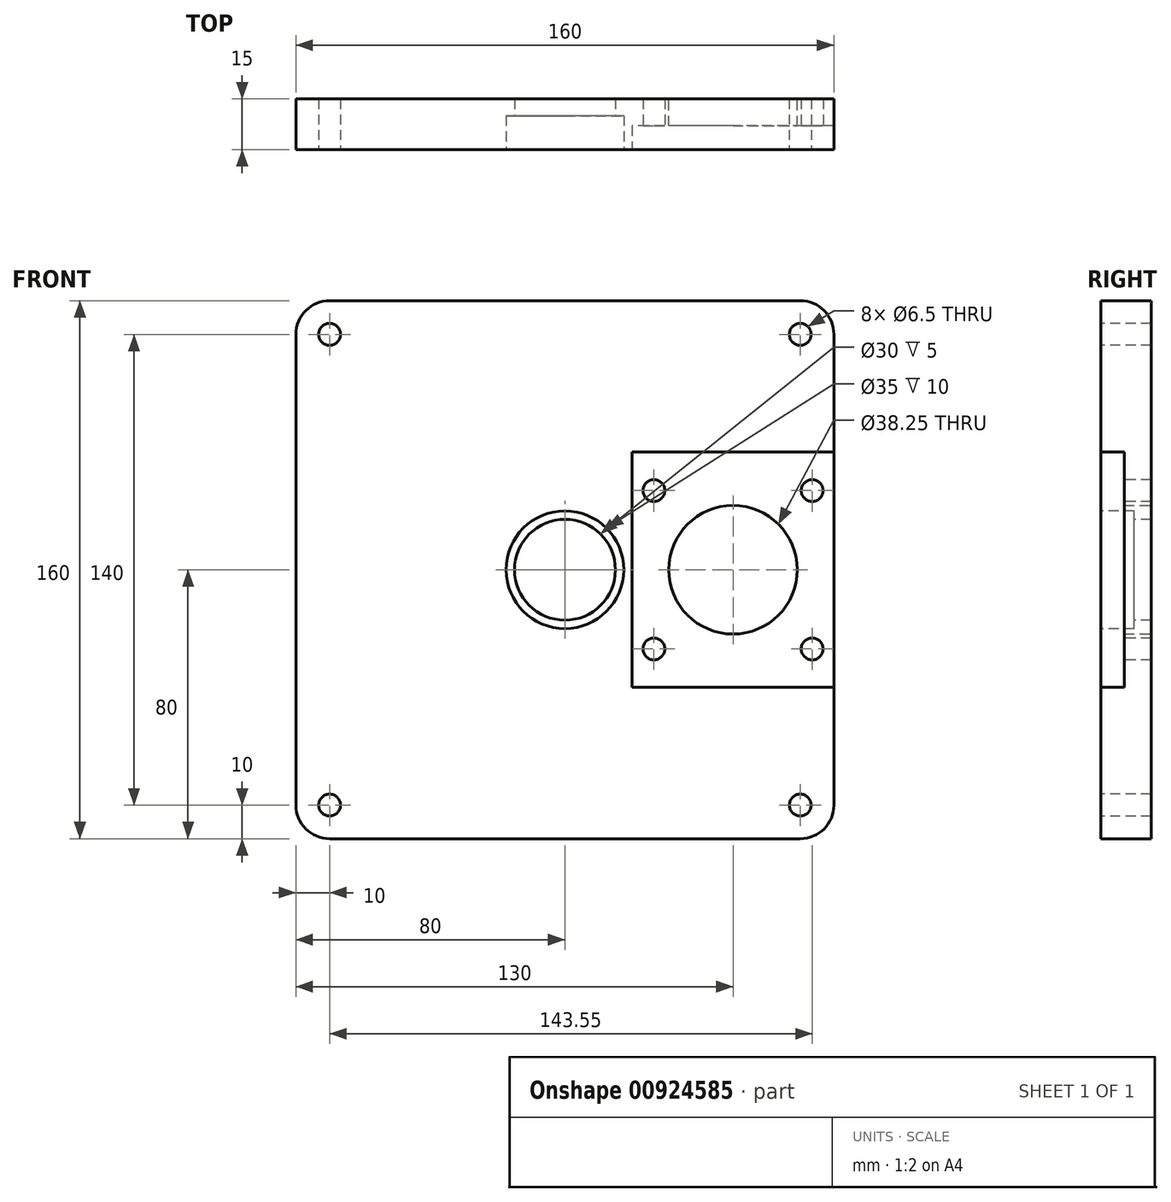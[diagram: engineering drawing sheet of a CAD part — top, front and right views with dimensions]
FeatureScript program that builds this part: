
annotation { "Feature Type Name" : "Feature", "Feature Type Description" : "" }
export const myFeature = defineFeature(function(context is Context, id is Id, definition is map)
    precondition{}
    {
        {
            var Q0;
            Q0=qCreatedBy(makeId("Front.planeOp"),FACE);
            var sketch = newSketch(context, id + "F0", { "sketchPlane" : qUnion([Q0])});
            skLineSegment(sketch, "E0.bottom", {"start": v(-80, 80) * mm, "end": v(80, 80) * mm});
            skLineSegment(sketch, "E0.top", {"start": v(-80, -80) * mm, "end": v(80, -80) * mm});
            skLineSegment(sketch, "E0.left", {"start": v(-80, 80) * mm, "end": v(-80, -80) * mm});
            skLineSegment(sketch, "E0.right", {"start": v(80, 80) * mm, "end": v(80, -80) * mm});
            skPoint(sketch, "E0.middle", {"position": v(0, 0) * mm});
            skSolve(sketch);
        }
        {
            var Q0;
            Q0=makeQuery(id+"F0.imprint","IMPRINT",FACE,{"disambiguationData":[TD([[makeQuery(id+"F0.imprint","IMPRINT",EDGE,{"derivedFrom":sQuery(id+"F0.wireOp",EDGE,"E0.bottom")}),-1.0]])]});
            extrude(context, id + "F1", {"entities" : qUnion([Q0]), "depth" : 15 * mm, "offsetDistance" : 25 * mm});
        }
        {
            var Q0;
            Q0=makeQuery(id+"F1.opExtrude","CAP_FACE",FACE,{"disambiguationData":[OSD([sQuery(id+"F0.wireOp",EDGE,"E0.bottom"),sQuery(id+"F0.wireOp",EDGE,"E0.top"),sQuery(id+"F0.wireOp",EDGE,"E0.left"),sQuery(id+"F0.wireOp",EDGE,"E0.right")])],"isStart":false});
            var sketch = newSketch(context, id + "F2", { "sketchPlane" : qUnion([Q0])});
            skCircle(sketch, "E1", {"center": v(0, 0) * mm, "radius": 15 * mm});
            skSolve(sketch);
        }
        {
            var Q0;
            Q0=makeQuery(id+"F2.imprint","IMPRINT",FACE,{"disambiguationData":[TD([[makeQuery(id+"F2.imprint","IMPRINT",EDGE,{"derivedFrom":sQuery(id+"F2.wireOp",EDGE,"E1")}),1.0]])]});
            extrude(context, id + "F3", {"entities" : qUnion([Q0]), "operationType" : NewBodyOperationType.REMOVE, "oppositeDirection" : true, "depth" : 25 * mm, "offsetDistance" : 25 * mm});
        }
        {
            var Q0;
            Q0=makeQuery(id+"F1.opExtrude","CAP_FACE",FACE,{"disambiguationData":[OSD([sQuery(id+"F0.wireOp",EDGE,"E0.bottom"),sQuery(id+"F0.wireOp",EDGE,"E0.top"),sQuery(id+"F0.wireOp",EDGE,"E0.left"),sQuery(id+"F0.wireOp",EDGE,"E0.right")])],"isStart":false});
            var sketch = newSketch(context, id + "F4", { "sketchPlane" : qUnion([Q0])});
            skCircle(sketch, "E2", {"center": v(0, 0) * mm, "radius": 17.5 * mm});
            skSolve(sketch);
        }
        {
            var Q0;
            Q0=makeQuery(id+"F4.imprint","IMPRINT",FACE,{"disambiguationData":[TD([[makeQuery(id+"F4.imprint","IMPRINT",EDGE,{"derivedFrom":sQuery(id+"F4.wireOp",EDGE,"E2")}),1.0]])]});
            extrude(context, id + "F5", {"entities" : qUnion([Q0]), "operationType" : NewBodyOperationType.REMOVE, "oppositeDirection" : true, "depth" : 10 * mm, "offsetDistance" : 25 * mm});
        }
        {
            var Q0;
            Q0=makeQuery(id+"F1.opExtrude","SWEPT_EDGE",EDGE,{"disambiguationData":[OSD([sQuery(id+"F0.wireOp",EDGE,"E0.bottom"),sQuery(id+"F0.wireOp",EDGE,"E0.right")])]});
            var Q1;
            Q1=makeQuery(id+"F1.opExtrude","SWEPT_EDGE",EDGE,{"disambiguationData":[OSD([sQuery(id+"F0.wireOp",EDGE,"E0.top"),sQuery(id+"F0.wireOp",EDGE,"E0.right")])]});
            var Q2;
            Q2=makeQuery(id+"F1.opExtrude","SWEPT_EDGE",EDGE,{"disambiguationData":[OSD([sQuery(id+"F0.wireOp",EDGE,"E0.top"),sQuery(id+"F0.wireOp",EDGE,"E0.left")])]});
            var Q3;
            Q3=makeQuery(id+"F1.opExtrude","SWEPT_EDGE",EDGE,{"disambiguationData":[OSD([sQuery(id+"F0.wireOp",EDGE,"E0.bottom"),sQuery(id+"F0.wireOp",EDGE,"E0.left")])]});
            fillet(context, id + "F6", {"entities" : qUnion([Q0, Q1, Q2, Q3]), "radius" : 10 * mm, "tangentPropagation" : true, "allowEdgeOverflow" : false});
        }
        {
            var Q0;
            Q0=makeQuery(id+"F1.opExtrude","CAP_FACE",FACE,{"disambiguationData":[OSD([sQuery(id+"F0.wireOp",EDGE,"E0.bottom"),sQuery(id+"F0.wireOp",EDGE,"E0.top"),sQuery(id+"F0.wireOp",EDGE,"E0.left"),sQuery(id+"F0.wireOp",EDGE,"E0.right")])],"isStart":false});
            var sketch = newSketch(context, id + "F7", { "sketchPlane" : qUnion([Q0])});
            skLineSegment(sketch, "E3.bottom", {"start": v(80, -35) * mm, "end": v(20, -35) * mm});
            skLineSegment(sketch, "E3.top", {"start": v(80, 35) * mm, "end": v(20, 35) * mm});
            skLineSegment(sketch, "E3.left", {"start": v(80, -35) * mm, "end": v(80, 35) * mm});
            skLineSegment(sketch, "E3.right", {"start": v(20, -35) * mm, "end": v(20, 35) * mm});
            skPoint(sketch, "E3.middle", {"position": v(50, 0) * mm});
            skSolve(sketch);
        }
        {
            var Q0;
            Q0=makeQuery(id+"F7.imprint","IMPRINT",FACE,{"disambiguationData":[TD([[makeQuery(id+"F7.imprint","IMPRINT",EDGE,{"derivedFrom":sQuery(id+"F7.wireOp",EDGE,"E3.bottom")}),-1.0]])]});
            extrude(context, id + "F8", {"entities" : qUnion([Q0]), "operationType" : NewBodyOperationType.REMOVE, "oppositeDirection" : true, "depth" : 7 * mm, "offsetDistance" : 25 * mm});
        }
        {
            var Q0;
            Q0=makeQuery(id+"F1.opExtrude","CAP_FACE",FACE,{"disambiguationData":[OSD([sQuery(id+"F0.wireOp",EDGE,"E0.bottom"),sQuery(id+"F0.wireOp",EDGE,"E0.top"),sQuery(id+"F0.wireOp",EDGE,"E0.left"),sQuery(id+"F0.wireOp",EDGE,"E0.right")])],"isStart":true});
            var sketch = newSketch(context, id + "F9", { "sketchPlane" : qUnion([Q0])});
            skCircle(sketch, "E4", {"center": v(-50, 0) * mm, "radius": 19.12 * mm});
            skSolve(sketch);
        }
        {
            var Q0;
            Q0=makeQuery(id+"F9.imprint","IMPRINT",FACE,{"disambiguationData":[TD([[makeQuery(id+"F9.imprint","IMPRINT",EDGE,{"derivedFrom":sQuery(id+"F9.wireOp",EDGE,"E4")}),1.0]])]});
            var Q1;
            Q1=sQuery(id+"F9.wireOp",EDGE,"E4");
            extrude(context, id + "F10", {"entities" : qUnion([Q0]), "operationType" : NewBodyOperationType.REMOVE, "surfaceEntities" : qUnion([Q1]), "oppositeDirection" : true, "depth" : 25 * mm, "offsetDistance" : 25 * mm});
        }
        {
            var Q0;
            Q0=makeQuery(id+"F8.boolean.opBoolean","COPY",FACE,{"derivedFrom":makeQuery(id+"F8.opExtrude","CAP_FACE",FACE,{"disambiguationData":[OSD([sQuery(id+"F7.wireOp",EDGE,"E3.bottom"),sQuery(id+"F7.wireOp",EDGE,"E3.top"),sQuery(id+"F7.wireOp",EDGE,"E3.left"),sQuery(id+"F7.wireOp",EDGE,"E3.right")])],"isStart":false})});
            var sketch = newSketch(context, id + "F11", { "sketchPlane" : qUnion([Q0])});
            skCircle(sketch, "E5", {"center": v(73.55, 23.55) * mm, "radius": 3.25 * mm});
            skCircle(sketch, "E6", {"center": v(26.45, 23.55) * mm, "radius": 3.25 * mm});
            skCircle(sketch, "E7", {"center": v(26.45, -23.55) * mm, "radius": 3.25 * mm});
            skCircle(sketch, "E8", {"center": v(73.55, -23.55) * mm, "radius": 3.25 * mm});
            skCircle(sketch, "E9.0", {"center": v(50, 0) * mm, "radius": 19.13 * mm});
            skSolve(sketch);
        }
        {
            var Q0;
            Q0=makeQuery(id+"F11.imprint","IMPRINT",FACE,{"disambiguationData":[TD([[makeQuery(id+"F11.imprint","IMPRINT",EDGE,{"derivedFrom":sQuery(id+"F11.wireOp",EDGE,"E6")}),1.0]])]});
            var Q1;
            Q1=makeQuery(id+"F11.imprint","IMPRINT",FACE,{"disambiguationData":[TD([[makeQuery(id+"F11.imprint","IMPRINT",EDGE,{"derivedFrom":sQuery(id+"F11.wireOp",EDGE,"E7")}),1.0]])]});
            var Q2;
            Q2=makeQuery(id+"F11.imprint","IMPRINT",FACE,{"disambiguationData":[TD([[makeQuery(id+"F11.imprint","IMPRINT",EDGE,{"derivedFrom":sQuery(id+"F11.wireOp",EDGE,"E8")}),1.0]])]});
            var Q3;
            Q3=makeQuery(id+"F11.imprint","IMPRINT",FACE,{"disambiguationData":[TD([[makeQuery(id+"F11.imprint","IMPRINT",EDGE,{"derivedFrom":sQuery(id+"F11.wireOp",EDGE,"E5")}),1.0]])]});
            extrude(context, id + "F12", {"entities" : qUnion([Q0, Q1, Q2, Q3]), "operationType" : NewBodyOperationType.REMOVE, "oppositeDirection" : true, "depth" : 25 * mm, "offsetDistance" : 25 * mm});
        }
        {
            var Q0;
            Q0=makeQuery(id+"F1.opExtrude","CAP_FACE",FACE,{"disambiguationData":[OSD([sQuery(id+"F0.wireOp",EDGE,"E0.bottom"),sQuery(id+"F0.wireOp",EDGE,"E0.top"),sQuery(id+"F0.wireOp",EDGE,"E0.left"),sQuery(id+"F0.wireOp",EDGE,"E0.right")])],"isStart":false});
            var sketch = newSketch(context, id + "F13", { "sketchPlane" : qUnion([Q0])});
            skCircle(sketch, "E10", {"center": v(70, 70) * mm, "radius": 3.25 * mm});
            skCircle(sketch, "E11", {"center": v(70, -70) * mm, "radius": 3.25 * mm});
            skCircle(sketch, "E12", {"center": v(-70, -70) * mm, "radius": 3.25 * mm});
            skCircle(sketch, "E13", {"center": v(-70, 70) * mm, "radius": 3.25 * mm});
            skSolve(sketch);
        }
        {
            var Q0;
            Q0=makeQuery(id+"F13.imprint","IMPRINT",FACE,{"disambiguationData":[TD([[makeQuery(id+"F13.imprint","IMPRINT",EDGE,{"derivedFrom":sQuery(id+"F13.wireOp",EDGE,"E10")}),1.0]])]});
            var Q1;
            Q1=makeQuery(id+"F13.imprint","IMPRINT",FACE,{"disambiguationData":[TD([[makeQuery(id+"F13.imprint","IMPRINT",EDGE,{"derivedFrom":sQuery(id+"F13.wireOp",EDGE,"E13")}),1.0]])]});
            var Q2;
            Q2=makeQuery(id+"F13.imprint","IMPRINT",FACE,{"disambiguationData":[TD([[makeQuery(id+"F13.imprint","IMPRINT",EDGE,{"derivedFrom":sQuery(id+"F13.wireOp",EDGE,"E12")}),1.0]])]});
            var Q3;
            Q3=makeQuery(id+"F13.imprint","IMPRINT",FACE,{"disambiguationData":[TD([[makeQuery(id+"F13.imprint","IMPRINT",EDGE,{"derivedFrom":sQuery(id+"F13.wireOp",EDGE,"E11")}),1.0]])]});
            extrude(context, id + "F14", {"entities" : qUnion([Q0, Q1, Q2, Q3]), "operationType" : NewBodyOperationType.REMOVE, "oppositeDirection" : true, "depth" : 25 * mm, "offsetDistance" : 25 * mm});
        }
    });
